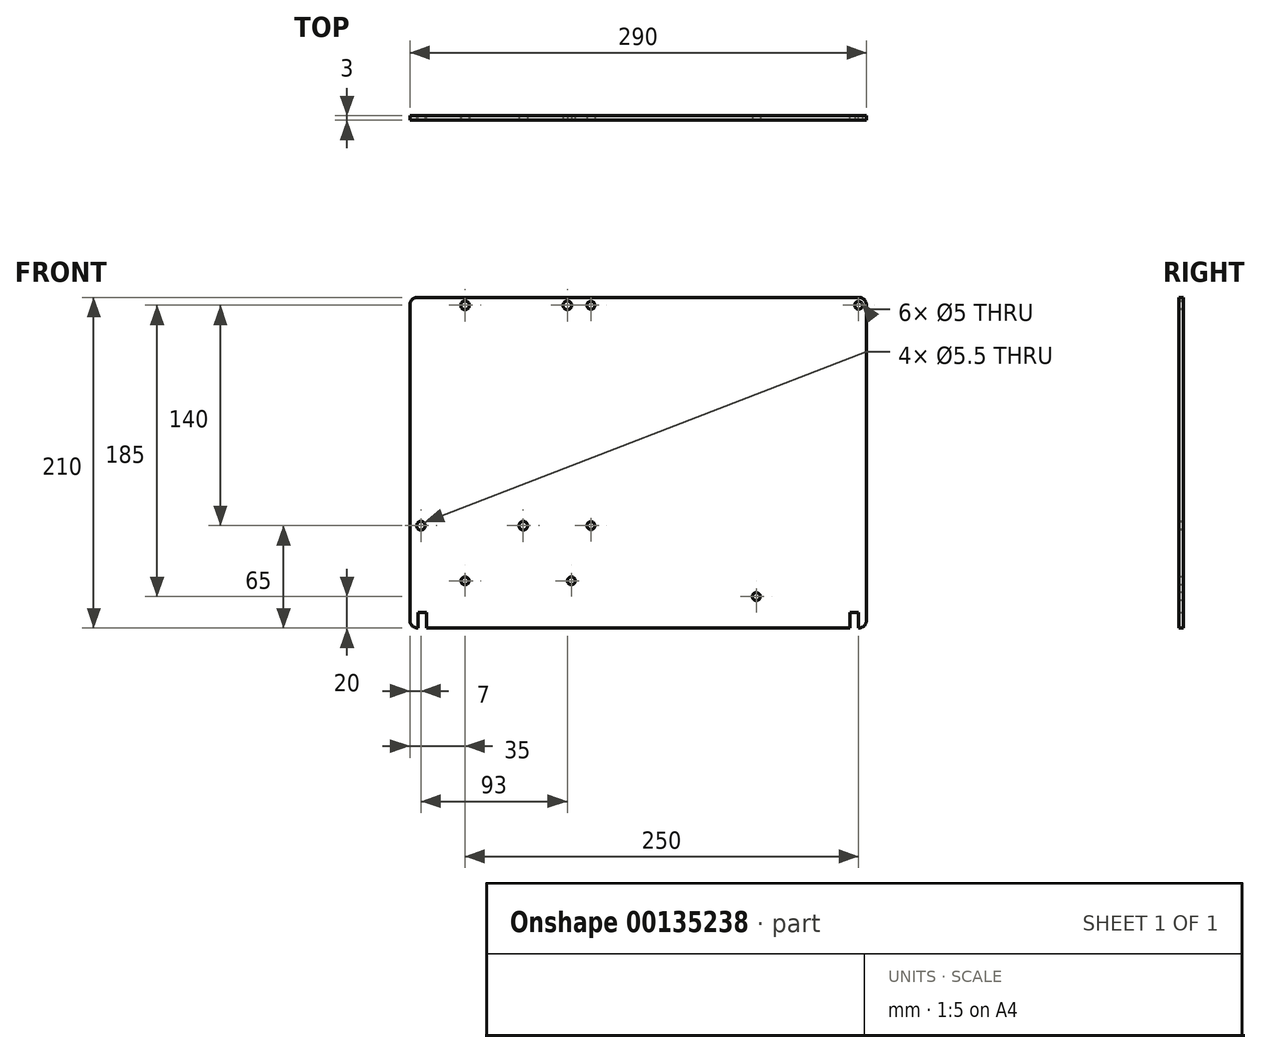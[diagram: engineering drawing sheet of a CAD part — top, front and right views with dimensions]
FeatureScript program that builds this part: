
annotation { "Feature Type Name" : "Feature", "Feature Type Description" : "" }
export const myFeature = defineFeature(function(context is Context, id is Id, definition is map)
    precondition{}
    {
        {
            var Q0;
            Q0=qCreatedBy(makeId("Front.planeOp"),FACE);
            var sketch = newSketch(context, id + "F0", { "sketchPlane" : qUnion([Q0])});
            skLineSegment(sketch, "E0.bottom", {"start": v(145, -105) * mm, "end": v(140, -105) * mm});
            skLineSegment(sketch, "E0.top", {"start": v(145, 105) * mm, "end": v(-145, 105) * mm});
            skLineSegment(sketch, "E0.left", {"start": v(145, -105) * mm, "end": v(145, 105) * mm});
            skLineSegment(sketch, "E0.right", {"start": v(-145, -105) * mm, "end": v(-145, 105) * mm});
            skPoint(sketch, "E0.middle", {"position": v(0, 0) * mm});
            skLineSegment(sketch, "E1", {"start": v(-140, -105) * mm, "end": v(-140, -95) * mm});
            skLineSegment(sketch, "E2", {"start": v(-140, -95) * mm, "end": v(-134.5, -95) * mm});
            skLineSegment(sketch, "E3", {"start": v(-134.5, -95) * mm, "end": v(-134.5, -105) * mm});
            skLineSegment(sketch, "E4", {"start": v(140, -105) * mm, "end": v(140, -95) * mm});
            skLineSegment(sketch, "E5", {"start": v(140, -95) * mm, "end": v(134.5, -95) * mm});
            skLineSegment(sketch, "E6", {"start": v(134.5, -95) * mm, "end": v(134.5, -105) * mm});
            skLineSegment(sketch, "E7.trimOffspring", {"start": v(-140, -105) * mm, "end": v(-145, -105) * mm});
            skLineSegment(sketch, "E8.trimOffspring", {"start": v(134.5, -105) * mm, "end": v(-134.5, -105) * mm});
            skSolve(sketch);
        }
        {
            var Q0;
            Q0=makeQuery(id+"F0.imprint","IMPRINT",FACE,{"disambiguationData":[TD([[makeQuery(id+"F0.imprint","IMPRINT",EDGE,{"derivedFrom":sQuery(id+"F0.wireOp",EDGE,"E0.bottom")}),-1.0]])]});
            extrude(context, id + "F1", {"entities" : qUnion([Q0]), "depth" : 3 * mm});
        }
        {
            var Q0;
            {var subQ0=sQuery(id+"F0.wireOp",EDGE,"E8.trimOffspring");var subQ1=sQuery(id+"F0.wireOp",EDGE,"E3");var subQ2=sQuery(id+"F0.wireOp",EDGE,"E4");var subQ3=sQuery(id+"F0.wireOp",EDGE,"E0.left");var subQ4=sQuery(id+"F0.wireOp",EDGE,"E0.bottom");var subQ5=sQuery(id+"F0.wireOp",EDGE,"E0.top");var subQ6=sQuery(id+"F0.wireOp",EDGE,"E7.trimOffspring");var subQ7=sQuery(id+"F0.wireOp",EDGE,"E0.right");var subQ8=sQuery(id+"F0.wireOp",EDGE,"E2");var subQ9=sQuery(id+"F0.wireOp",EDGE,"E1");var subQ10=sQuery(id+"F0.wireOp",EDGE,"E5");var subQ11=sQuery(id+"F0.wireOp",EDGE,"E6");Q0=makeQuery(id+"Fkeax6t5Ps2Em87_1.boolean.opBoolean","SPLIT",FACE,{"disambiguationData":[TD([makeQuery(id+"F1.opExtrude","SWEPT_FACE",FACE,{"disambiguationData":[OSD([subQ4])]})])],"derivedFrom":makeQuery(id+"F1.opExtrude","CAP_FACE",FACE,{"disambiguationData":[OSD([subQ4,subQ5,subQ3,subQ7,subQ9,subQ8,subQ1,subQ2,subQ10,subQ11,subQ6,subQ0])],"isStart":false})});}
            var sketch = newSketch(context, id + "F2", { "sketchPlane" : qUnion([Q0])});
            skCircle(sketch, "E9", {"center": v(-110, 100) * mm, "radius": 2.75 * mm});
            skCircle(sketch, "E10", {"center": v(-138, -40) * mm, "radius": 2.75 * mm});
            skCircle(sketch, "E11", {"center": v(-45, 100) * mm, "radius": 2.75 * mm});
            skCircle(sketch, "E12", {"center": v(-73, -40) * mm, "radius": 2.75 * mm});
            skSolve(sketch);
        }
        {
            var Q0;
            Q0 = qSketchRegion(id + "F2", true);
            extrude(context, id + "F3", {"entities" : qUnion([Q0]), "operationType" : NewBodyOperationType.REMOVE, "endBound" : BoundingType.UP_TO_NEXT, "oppositeDirection" : true, "depth" : 25 * mm});
        }
        {
            var Q0;
            Q0=makeQuery(id+"F1.opExtrude","CAP_FACE",FACE,{"disambiguationData":[OSD([sQuery(id+"F0.wireOp",EDGE,"E0.bottom"),sQuery(id+"F0.wireOp",EDGE,"E0.top"),sQuery(id+"F0.wireOp",EDGE,"E0.left"),sQuery(id+"F0.wireOp",EDGE,"E0.right"),sQuery(id+"F0.wireOp",EDGE,"E1"),sQuery(id+"F0.wireOp",EDGE,"E2"),sQuery(id+"F0.wireOp",EDGE,"E3"),sQuery(id+"F0.wireOp",EDGE,"E4"),sQuery(id+"F0.wireOp",EDGE,"E5"),sQuery(id+"F0.wireOp",EDGE,"E6"),sQuery(id+"F0.wireOp",EDGE,"E7.trimOffspring"),sQuery(id+"F0.wireOp",EDGE,"E8.trimOffspring")])],"isStart":false});
            var sketch = newSketch(context, id + "F4", { "sketchPlane" : qUnion([Q0])});
            skCircle(sketch, "E13", {"center": v(-30, 100) * mm, "radius": 2.5 * mm});
            skCircle(sketch, "E14", {"center": v(140, 100) * mm, "radius": 2.5 * mm});
            skCircle(sketch, "E15", {"center": v(75, -85) * mm, "radius": 2.5 * mm});
            skCircle(sketch, "E16", {"center": v(-30, -40) * mm, "radius": 2.5 * mm});
            skSolve(sketch);
        }
        {
            var Q0;
            Q0 = qSketchRegion(id + "F4", true);
            extrude(context, id + "F5", {"entities" : qUnion([Q0]), "operationType" : NewBodyOperationType.REMOVE, "endBound" : BoundingType.UP_TO_NEXT, "oppositeDirection" : true, "depth" : 25 * mm});
        }
        {
            var Q0;
            Q0=makeQuery(id+"F1.opExtrude","CAP_FACE",FACE,{"disambiguationData":[OSD([sQuery(id+"F0.wireOp",EDGE,"E0.bottom"),sQuery(id+"F0.wireOp",EDGE,"E0.top"),sQuery(id+"F0.wireOp",EDGE,"E0.left"),sQuery(id+"F0.wireOp",EDGE,"E0.right"),sQuery(id+"F0.wireOp",EDGE,"E1"),sQuery(id+"F0.wireOp",EDGE,"E2"),sQuery(id+"F0.wireOp",EDGE,"E3"),sQuery(id+"F0.wireOp",EDGE,"E4"),sQuery(id+"F0.wireOp",EDGE,"E5"),sQuery(id+"F0.wireOp",EDGE,"E6"),sQuery(id+"F0.wireOp",EDGE,"E7.trimOffspring"),sQuery(id+"F0.wireOp",EDGE,"E8.trimOffspring")])],"isStart":false});
            var sketch = newSketch(context, id + "F6", { "sketchPlane" : qUnion([Q0])});
            skCircle(sketch, "E17", {"center": v(-110, -75) * mm, "radius": 2.5 * mm});
            skCircle(sketch, "E18", {"center": v(-42.5, -75) * mm, "radius": 2.5 * mm});
            skSolve(sketch);
        }
        {
            var Q0;
            Q0 = qSketchRegion(id + "F6", true);
            extrude(context, id + "F7", {"entities" : qUnion([Q0]), "operationType" : NewBodyOperationType.REMOVE, "endBound" : BoundingType.UP_TO_NEXT, "oppositeDirection" : true, "depth" : 25 * mm});
        }
        {
            var Q0;
            Q0=makeQuery(id+"F1.opExtrude","SWEPT_EDGE",EDGE,{"disambiguationData":[OSD([sQuery(id+"F0.wireOp",EDGE,"E0.top"),sQuery(id+"F0.wireOp",EDGE,"E0.right")])]});
            var Q1;
            Q1=makeQuery(id+"F1.opExtrude","SWEPT_EDGE",EDGE,{"disambiguationData":[OSD([sQuery(id+"F0.wireOp",EDGE,"E0.top"),sQuery(id+"F0.wireOp",EDGE,"E0.left")])]});
            var Q2;
            Q2=makeQuery(id+"F1.opExtrude","SWEPT_EDGE",EDGE,{"disambiguationData":[OSD([sQuery(id+"F0.wireOp",EDGE,"E0.bottom"),sQuery(id+"F0.wireOp",EDGE,"E0.left")])]});
            var Q3;
            Q3=makeQuery(id+"F1.opExtrude","SWEPT_EDGE",EDGE,{"disambiguationData":[OSD([sQuery(id+"F0.wireOp",EDGE,"E0.right"),sQuery(id+"F0.wireOp",EDGE,"E7.trimOffspring")])]});
            fillet(context, id + "F8", {"entities" : qUnion([Q0, Q1, Q2, Q3]), "radius" : 5 * mm, "tangentPropagation" : true, "allowEdgeOverflow" : false});
        }
    });
